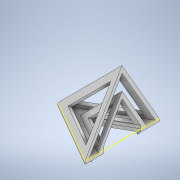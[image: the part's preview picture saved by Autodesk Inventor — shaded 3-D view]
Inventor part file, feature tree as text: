
AUTODESK INVENTOR PART (.ipt)
format: ipt  version: 2020 (Build 240168000, 168)  size: 218,112 bytes
history: native  units: mm
features: sketch x11, extrude x9, plane x4, split x2, shell x2, draft x1
ambient origin geometry x8: Origin, YZ Plane, XZ Plane, XY Plane, X Axis, Y Axis, Z Axis, Center Point
bodies: Solid1 (feature_tree), Solid2 (feature_tree)
feature tree (29):
  sketch  "Sketch1"  dims[d0=50.0mm d1=50.0mm]
  extrude  "Extrusion1"  Depth=50.0mm
  sketch  "Sketch3"  dims[d7=5.25mm d8=5.25mm d9=5.25mm]
  plane  "Work Plane1"
  plane  "Work Plane2"
  extrude  "Extrusion2"  Depth=2.0mm TaperAngle=0.0deg
  split  "Split1"
  shell  "Shell1"  Thickness=2.0mm
  sketch  "Sketch4"  dims[d10=2.0mm d11=0.0mm d12=2.0mm]
  sketch  "Sketch5"  dims[d13=5.0mm d14=5.0mm]
  plane  "Work Plane3"
  plane  "Work Plane4"
  extrude  "Extrusion3"  Depth=5.25mm
  split  "Split2"
  shell  "Shell2"  Thickness=5.25mm
  extrude  "Extrusion4"  Depth=2.0mm
  extrude  "Extrusion5"  Depth=5.0mm
  extrude  "Extrusion6"  Depth=2.0mm TaperAngle=0.0deg
  extrude  "Extrusion7"  Depth=5.0mm
  extrude  "Extrusion8"  Depth=2.0mm TaperAngle=0.0deg
  extrude  "Extrusion9"  Depth=4.0mm
  draft  "FaceDraft1"
  sketch  "Sketch2"  dims[d2=2.0mm d3=0.0mm d4=2.0mm d5=0.0mm d6=2.0mm]
  sketch  "Sketch6"  dims[d15=5.0mm d16=2.0mm d17=0.0mm]
  sketch  "Sketch7"  dims[d18=5.0mm d19=5.0mm]
  sketch  "Sketch8"  dims[d20=5.0mm d21=2.0mm d22=0.0mm]
  sketch  "Sketch9"  dims[d23=4.0mm d24=4.0mm]
  sketch  "Sketch10"  dims[d25=4.0mm]
  sketch  "Sketch11"  dims[d26=2.0mm d27=0.0mm d28=4.0mm d29=4.0mm d30=4.0mm d31=2.0mm d32=0.0mm d33=6.0mm d34=0.0mm d35=1.25mm d36=1.25mm d37=1.25mm d38=5.0mm d39=0.0mm d40=1.745329mm]
